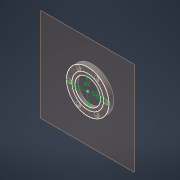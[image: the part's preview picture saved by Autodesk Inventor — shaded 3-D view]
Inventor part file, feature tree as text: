
AUTODESK INVENTOR PART (.ipt)
format: ipt  version: 2022 (Build 260153000, 153)  size: 134,656 bytes
history: native  units: mm
features: sketch x2, extrude x2, other x2, plane x1, hole x1
ambient origin geometry x8: Origin, YZ Plane, XZ Plane, XY Plane, X Axis, Y Axis, Z Axis, Center Point
bodies: Solid1 (feature_tree)
feature tree (8):
  plane  "Work Plane1"
  sketch  "Sketch1"  dims[d0=52.0mm d1=80.0mm]
  extrude  "Extrusion1"  Depth=80.0mm
  extrude  "Extrusion2"  Depth=8.0mm
  hole  "Hole1"  [1 undecoded]
  sketch  "Sketch2"  dims[d2=5.5mm d3=0.0mm d4=42.0mm d5=8.0mm d6=0.0mm d7=65.0mm d8=60.0mm d10=360.0deg d12=4.5mm d13=6.0mm d14=8.0mm d15=4.6mm d16=14.3117mm d17=8.0mm d18=20.594885mm]
  other  "SistemaDeElevación.iam"
  other  "soporte de rodamientos:1"
note: 1 required parameter value undecoded (feature->parameter linkage not recoverable at this tier; creation-order binding heuristic only, values carry confidence <= 0.55)
